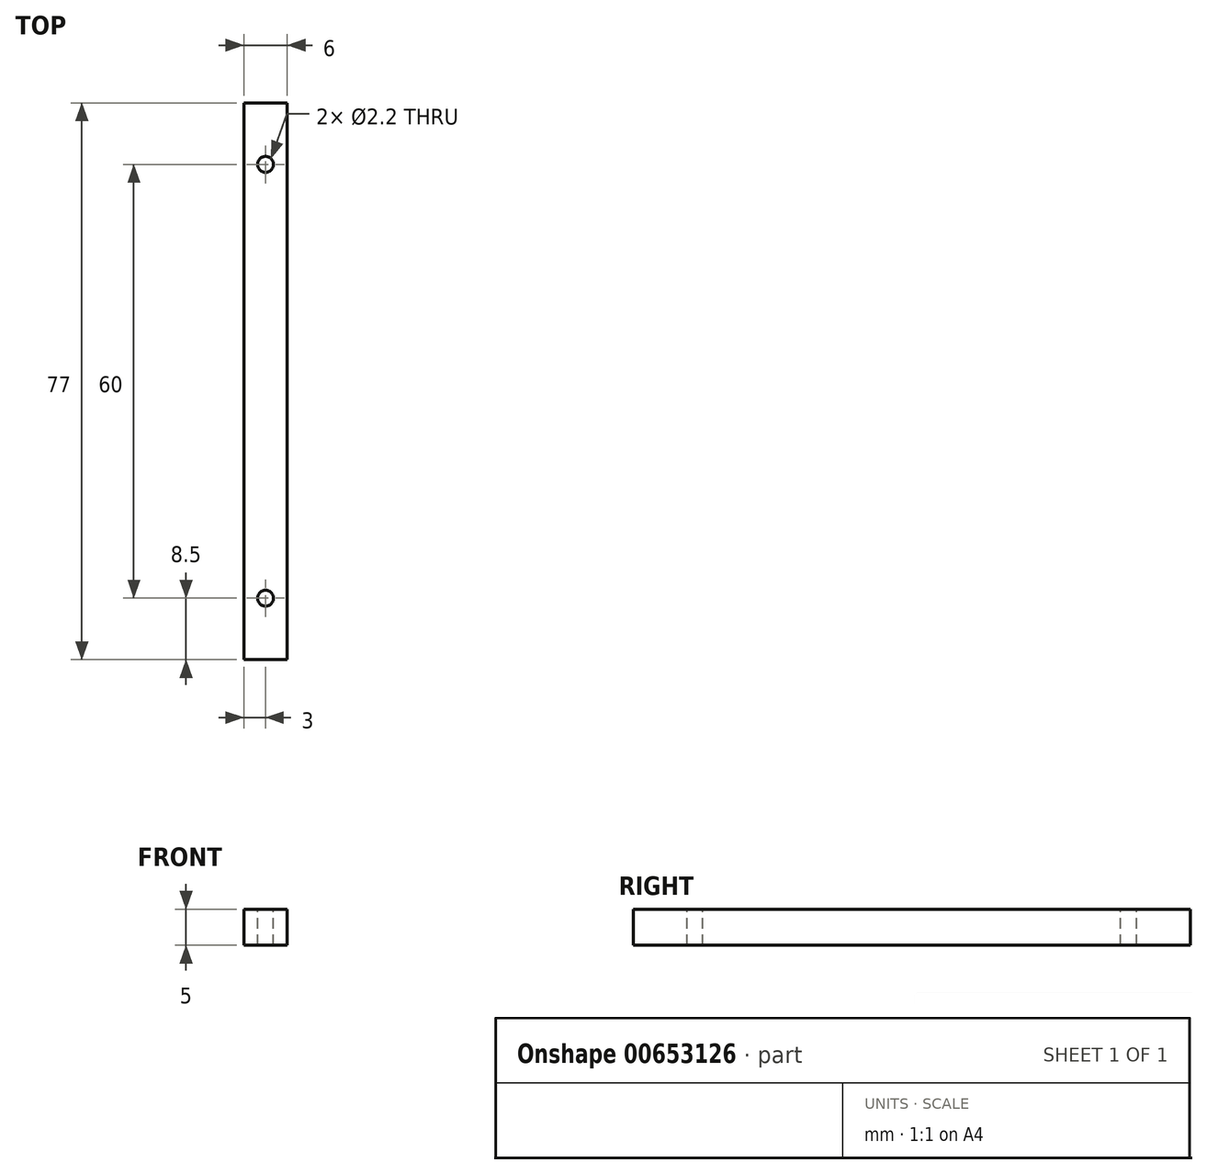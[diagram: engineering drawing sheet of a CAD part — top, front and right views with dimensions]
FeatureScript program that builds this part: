
annotation { "Feature Type Name" : "Feature", "Feature Type Description" : "" }
export const myFeature = defineFeature(function(context is Context, id is Id, definition is map)
    precondition{}
    {
        {
            var Q0;
            Q0=qCreatedBy(makeId("Front.planeOp"),FACE);
            var sketch = newSketch(context, id + "F0", { "sketchPlane" : qUnion([Q0])});
            skLineSegment(sketch, "E0.bottom", {"start": v(0, 0) * mm, "end": v(6, 0) * mm});
            skLineSegment(sketch, "E0.top", {"start": v(0, 5) * mm, "end": v(6, 5) * mm});
            skLineSegment(sketch, "E0.left", {"start": v(0, 0) * mm, "end": v(0, 5) * mm});
            skLineSegment(sketch, "E0.right", {"start": v(6, 0) * mm, "end": v(6, 5) * mm});
            skSolve(sketch);
        }
        {
            var Q0;
            Q0 = qSketchRegion(id + "F0", true);
            extrude(context, id + "F1", {"entities" : qUnion([Q0]), "depth" : 77 * mm, "offsetDistance" : 25 * mm});
        }
        {
            var Q0;
            Q0=makeQuery(id+"F1.opExtrude","SWEPT_FACE",FACE,{"disambiguationData":[OSD([sQuery(id+"F0.wireOp",EDGE,"E0.top")])]});
            var sketch = newSketch(context, id + "F2", { "sketchPlane" : qUnion([Q0])});
            skLineSegment(sketch, "E1", {"start": v(3, 12.72) * mm, "end": v(3, -96.85) * mm, "construction": true});
            skLineSegment(sketch, "E2", {"start": v(-23.13, -38.5) * mm, "end": v(33.2, -38.5) * mm, "construction": true});
            skCircle(sketch, "E3", {"center": v(3, -8.5) * mm, "radius": 1.1 * mm});
            skCircle(sketch, "E4", {"center": v(3, -68.5) * mm, "radius": 1.1 * mm});
            skSolve(sketch);
        }
        {
            var Q0;
            Q0 = qSketchRegion(id + "F2", true);
            extrude(context, id + "F3", {"entities" : qUnion([Q0]), "operationType" : NewBodyOperationType.REMOVE, "oppositeDirection" : true, "depth" : 25 * mm, "offsetDistance" : 25 * mm});
        }
    });
